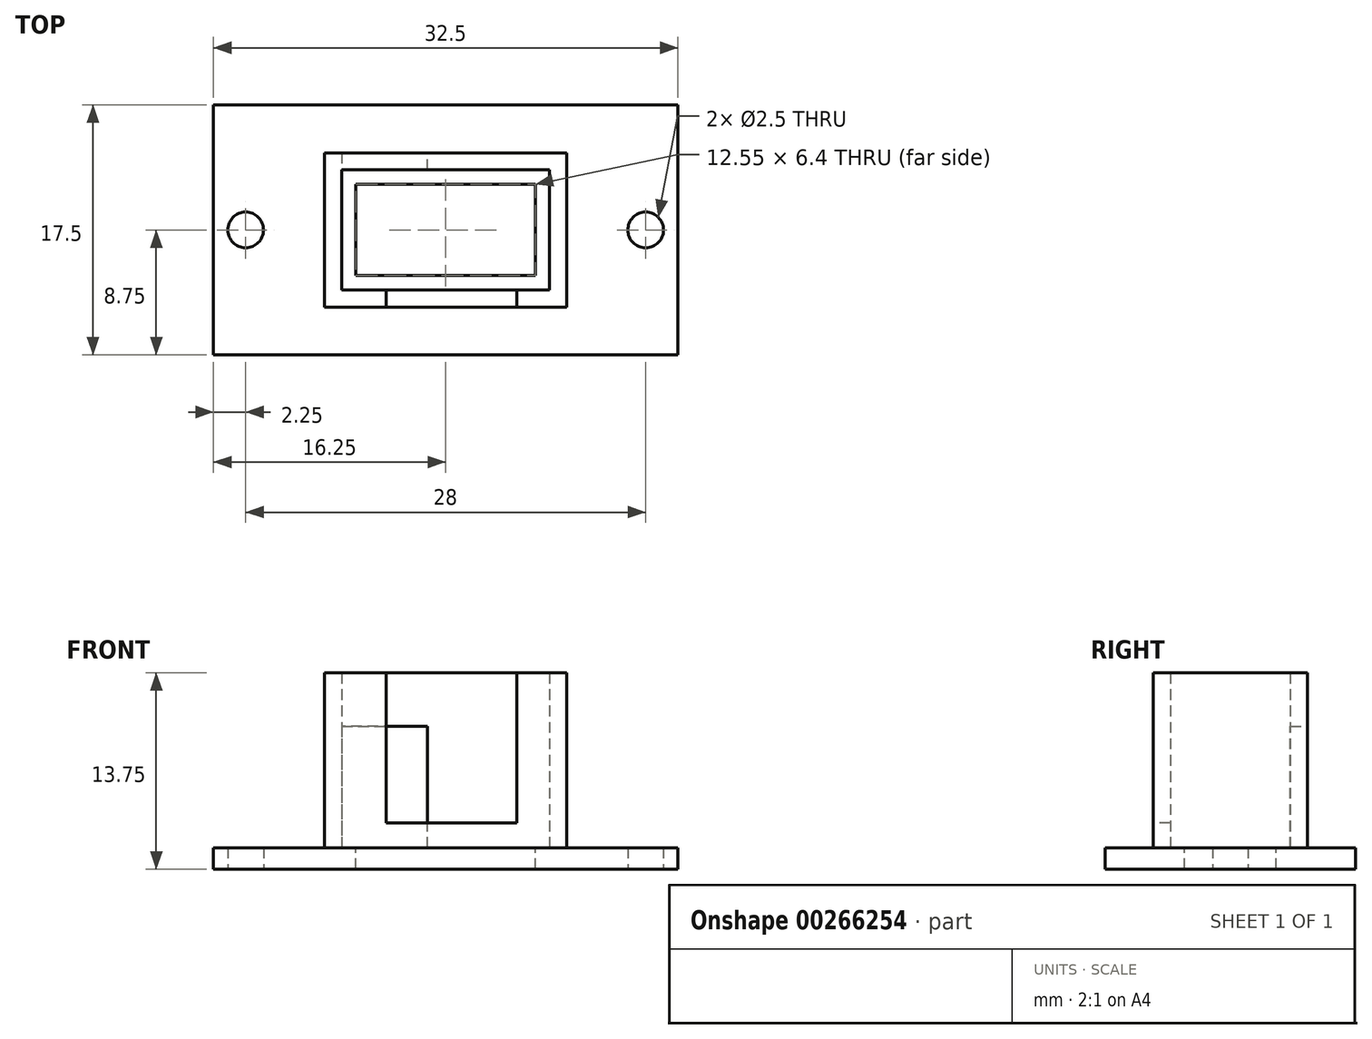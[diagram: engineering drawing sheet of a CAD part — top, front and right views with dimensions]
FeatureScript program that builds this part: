
annotation { "Feature Type Name" : "Feature", "Feature Type Description" : "" }
export const myFeature = defineFeature(function(context is Context, id is Id, definition is map)
    precondition{}
    {
        {
            var Q0;
            Q0=qCreatedBy(makeId("Top.planeOp"),FACE);
            var sketch = newSketch(context, id + "F0", { "sketchPlane" : qUnion([Q0])});
            skLineSegment(sketch, "E0.bottom", {"start": v(-16.25, 8.75) * mm, "end": v(16.25, 8.75) * mm});
            skLineSegment(sketch, "E0.top", {"start": v(-16.25, -8.75) * mm, "end": v(16.25, -8.75) * mm});
            skLineSegment(sketch, "E0.left", {"start": v(-16.25, 8.75) * mm, "end": v(-16.25, -8.75) * mm});
            skLineSegment(sketch, "E0.right", {"start": v(16.25, 8.75) * mm, "end": v(16.25, -8.75) * mm});
            skCircle(sketch, "E1", {"center": v(14, 0) * mm, "radius": 1.25 * mm});
            skCircle(sketch, "E2", {"center": v(-14, 0) * mm, "radius": 1.25 * mm});
            skSolve(sketch);
        }
        {
            var Q0;
            Q0=makeQuery(id+"F0.imprint","IMPRINT",FACE,{"disambiguationData":[TD([[makeQuery(id+"F0.imprint","IMPRINT",EDGE,{"derivedFrom":sQuery(id+"F0.wireOp",EDGE,"E0.bottom")}),-1.0]])]});
            extrude(context, id + "F1", {"entities" : qUnion([Q0]), "depth" : 1.5 * mm});
        }
        {
            var Q0;
            Q0=makeQuery(id+"F1.opExtrude","CAP_FACE",FACE,{"disambiguationData":[OSD([sQuery(id+"F0.wireOp",EDGE,"E0.bottom"),sQuery(id+"F0.wireOp",EDGE,"E0.top"),sQuery(id+"F0.wireOp",EDGE,"E0.left"),sQuery(id+"F0.wireOp",EDGE,"E0.right"),sQuery(id+"F0.wireOp",EDGE,"E1"),sQuery(id+"F0.wireOp",EDGE,"E2")])],"isStart":false});
            var sketch = newSketch(context, id + "F2", { "sketchPlane" : qUnion([Q0])});
            skLineSegment(sketch, "E3.bottom", {"start": v(-7.28, 4.2) * mm, "end": v(7.28, 4.2) * mm});
            skLineSegment(sketch, "E3.top", {"start": v(-7.28, -4.2) * mm, "end": v(7.28, -4.2) * mm});
            skLineSegment(sketch, "E3.left", {"start": v(-7.28, 4.2) * mm, "end": v(-7.28, -4.2) * mm});
            skLineSegment(sketch, "E3.right", {"start": v(7.28, 4.2) * mm, "end": v(7.28, -4.2) * mm});
            skLineSegment(sketch, "E4.0", {"start": v(-8.47, 5.4) * mm, "end": v(-8.47, -5.4) * mm});
            skLineSegment(sketch, "E4.1", {"start": v(-8.47, 5.4) * mm, "end": v(8.47, 5.4) * mm});
            skLineSegment(sketch, "E4.2", {"start": v(8.47, 5.4) * mm, "end": v(8.47, -5.4) * mm});
            skLineSegment(sketch, "E4.3", {"start": v(-8.47, -5.4) * mm, "end": v(8.47, -5.4) * mm});
            skSolve(sketch);
        }
        {
            var Q0;
            Q0=makeQuery(id+"F2.imprint","IMPRINT",FACE,{"disambiguationData":[TD([[makeQuery(id+"F2.imprint","IMPRINT",EDGE,{"derivedFrom":sQuery(id+"F2.wireOp",EDGE,"E3.bottom")}),1.0]])]});
            extrude(context, id + "F3", {"entities" : qUnion([Q0]), "operationType" : NewBodyOperationType.ADD, "depth" : 12.25 * mm});
        }
        {
            var Q0;
            Q0=makeQuery(id+"F3.opExtrude","SWEPT_FACE",FACE,{"disambiguationData":[OSD([sQuery(id+"F2.wireOp",EDGE,"E4.3")])]});
            var sketch = newSketch(context, id + "F4", { "sketchPlane" : qUnion([Q0])});
            skLineSegment(sketch, "E5.bottom", {"start": v(-4.18, 13.75) * mm, "end": v(4.98, 13.75) * mm});
            skLineSegment(sketch, "E5.top", {"start": v(-4.18, 3.25) * mm, "end": v(4.98, 3.25) * mm});
            skLineSegment(sketch, "E5.left", {"start": v(-4.18, 13.75) * mm, "end": v(-4.18, 3.25) * mm});
            skLineSegment(sketch, "E5.right", {"start": v(4.98, 13.75) * mm, "end": v(4.98, 3.25) * mm});
            skSolve(sketch);
        }
        {
            var Q0;
            Q0=makeQuery(id+"F4.imprint","IMPRINT",FACE,{"disambiguationData":[TD([[makeQuery(id+"F4.imprint","IMPRINT",EDGE,{"derivedFrom":sQuery(id+"F4.wireOp",EDGE,"E5.bottom")}),-1.0]])]});
            var Q1;
            Q1=makeQuery(id+"F3.opExtrude","SWEPT_FACE",FACE,{"disambiguationData":[OSD([sQuery(id+"F2.wireOp",EDGE,"E3.top")])]});
            extrude(context, id + "F5", {"entities" : qUnion([Q0]), "operationType" : NewBodyOperationType.REMOVE, "endBound" : BoundingType.UP_TO_SURFACE, "oppositeDirection" : true, "endBoundEntityFace" : qUnion([Q1]), "depth" : 25 * mm});
        }
        {
            var Q0;
            Q0=makeQuery(id+"F3.opExtrude","SWEPT_FACE",FACE,{"disambiguationData":[OSD([sQuery(id+"F2.wireOp",EDGE,"E4.1")])]});
            var sketch = newSketch(context, id + "F6", { "sketchPlane" : qUnion([Q0])});
            skLineSegment(sketch, "E6.bottom", {"start": v(1.27, 10) * mm, "end": v(7.27, 10) * mm});
            skLineSegment(sketch, "E6.top", {"start": v(1.27, 1.5) * mm, "end": v(7.27, 1.5) * mm});
            skLineSegment(sketch, "E6.left", {"start": v(1.27, 10) * mm, "end": v(1.27, 1.5) * mm});
            skLineSegment(sketch, "E6.right", {"start": v(7.27, 10) * mm, "end": v(7.27, 1.5) * mm});
            skSolve(sketch);
        }
        {
            var Q0;
            Q0=makeQuery(id+"F6.imprint","IMPRINT",FACE,{"disambiguationData":[TD([[makeQuery(id+"F6.imprint","IMPRINT",EDGE,{"derivedFrom":sQuery(id+"F6.wireOp",EDGE,"E6.bottom")}),-1.0]])]});
            var Q1;
            Q1=makeQuery(id+"F3.opExtrude","SWEPT_FACE",FACE,{"disambiguationData":[OSD([sQuery(id+"F2.wireOp",EDGE,"E3.bottom")])]});
            extrude(context, id + "F7", {"entities" : qUnion([Q0]), "operationType" : NewBodyOperationType.REMOVE, "endBound" : BoundingType.UP_TO_SURFACE, "oppositeDirection" : true, "endBoundEntityFace" : qUnion([Q1]), "depth" : 25 * mm});
        }
        {
            var Q0;
            {var subQ0=sQuery(id+"F0.wireOp",EDGE,"E2");var subQ1=sQuery(id+"F0.wireOp",EDGE,"E1");var subQ2=sQuery(id+"F0.wireOp",EDGE,"E0.right");var subQ3=sQuery(id+"F0.wireOp",EDGE,"E0.left");var subQ4=sQuery(id+"F0.wireOp",EDGE,"E0.top");var subQ5=sQuery(id+"F0.wireOp",EDGE,"E0.bottom");var subQ6=makeQuery(id+"F1.opExtrude","CAP_FACE",FACE,{"disambiguationData":[OSD([subQ5,subQ4,subQ3,subQ2,subQ1,subQ0])],"isStart":false});Q0=makeQuery(id+"F7.boolean.opBoolean","MERGE",FACE,{"derivedFrom":[makeQuery(id+"F3.boolean.opBoolean","SPLIT",FACE,{"disambiguationData":[TD([makeQuery(id+"F1.opExtrude","SWEPT_FACE",FACE,{"disambiguationData":[OSD([subQ5])]})])],"derivedFrom":subQ6}),makeQuery(id+"F3.boolean.opBoolean","SPLIT",FACE,{"disambiguationData":[TD([makeQuery(id+"F3.opExtrude","SWEPT_FACE",FACE,{"disambiguationData":[OSD([sQuery(id+"F2.wireOp",EDGE,"E3.bottom")])]})])],"derivedFrom":subQ6}),makeQuery(id+"F7.opExtrude","SWEPT_FACE",FACE,{"disambiguationData":[OSD([sQuery(id+"F6.wireOp",EDGE,"E6.top")])]})]});}
            var sketch = newSketch(context, id + "F8", { "sketchPlane" : qUnion([Q0])});
            skLineSegment(sketch, "E7.bottom", {"start": v(-6.28, 3.2) * mm, "end": v(6.28, 3.2) * mm});
            skLineSegment(sketch, "E7.top", {"start": v(-6.28, -3.2) * mm, "end": v(6.28, -3.2) * mm});
            skLineSegment(sketch, "E7.left", {"start": v(-6.28, 3.2) * mm, "end": v(-6.28, -3.2) * mm});
            skLineSegment(sketch, "E7.right", {"start": v(6.28, 3.2) * mm, "end": v(6.28, -3.2) * mm});
            skSolve(sketch);
        }
        {
            var Q0;
            Q0=makeQuery(id+"F8.imprint","IMPRINT",FACE,{"disambiguationData":[TD([[makeQuery(id+"F8.imprint","IMPRINT",EDGE,{"derivedFrom":sQuery(id+"F8.wireOp",EDGE,"E7.bottom")}),-1.0]])]});
            extrude(context, id + "F9", {"entities" : qUnion([Q0]), "operationType" : NewBodyOperationType.REMOVE, "oppositeDirection" : true, "depth" : 25 * mm});
        }
    });
